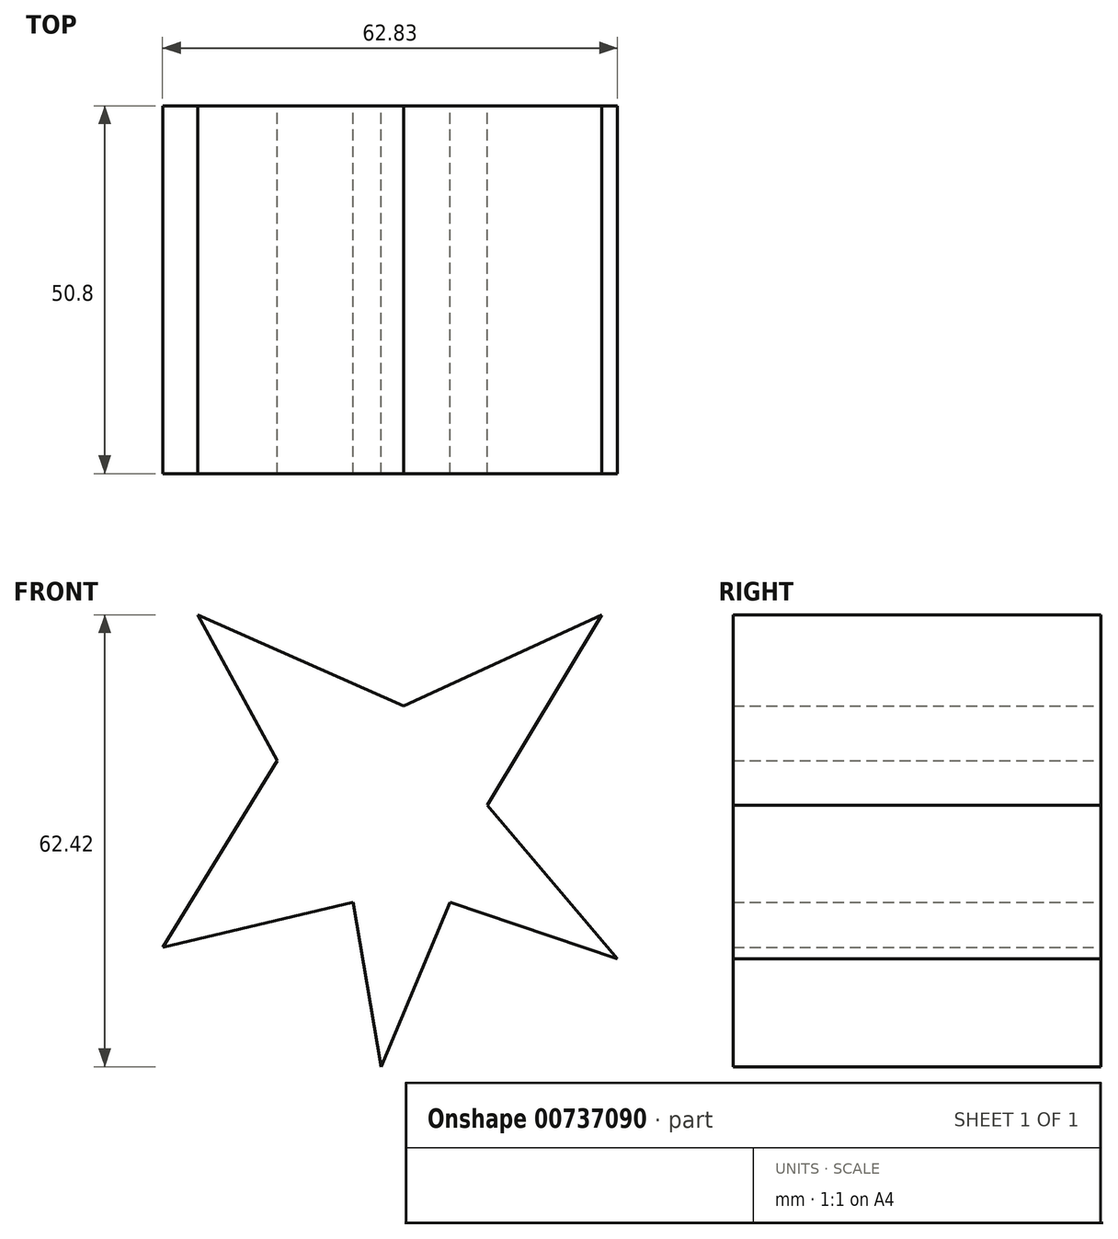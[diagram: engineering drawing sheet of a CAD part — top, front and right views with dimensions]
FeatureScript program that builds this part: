
annotation { "Feature Type Name" : "Feature", "Feature Type Description" : "" }
export const myFeature = defineFeature(function(context is Context, id is Id, definition is map)
    precondition{}
    {
        {
            var Q0;
            Q0=qCreatedBy(makeId("Front.planeOp"),FACE);
            var sketch = newSketch(context, id + "F0", { "sketchPlane" : qUnion([Q0])});
            skLineSegment(sketch, "E0", {"start": v(0, 0) * mm, "end": v(9.53, 22.69) * mm});
            skLineSegment(sketch, "E1", {"start": v(9.53, 22.69) * mm, "end": v(32.62, 14.9) * mm});
            skLineSegment(sketch, "E2", {"start": v(32.62, 14.9) * mm, "end": v(14.63, 36.11) * mm});
            skLineSegment(sketch, "E3", {"start": v(14.63, 36.11) * mm, "end": v(30.47, 62.42) * mm});
            skLineSegment(sketch, "E4", {"start": v(30.47, 62.42) * mm, "end": v(3.09, 49.8) * mm});
            skLineSegment(sketch, "E5", {"start": v(3.09, 49.8) * mm, "end": v(-25.37, 62.42) * mm});
            skLineSegment(sketch, "E6", {"start": v(-25.37, 62.42) * mm, "end": v(-14.36, 42.29) * mm});
            skLineSegment(sketch, "E7", {"start": v(-14.36, 42.29) * mm, "end": v(-30.2, 16.51) * mm});
            skLineSegment(sketch, "E8", {"start": v(-30.2, 16.51) * mm, "end": v(-3.9, 22.69) * mm});
            skLineSegment(sketch, "E9", {"start": v(-3.9, 22.69) * mm, "end": v(0, 0) * mm});
            skSolve(sketch);
        }
        {
            var Q0;
            Q0=makeQuery(id+"F0.imprint","IMPRINT",FACE,{"disambiguationData":[TD([[makeQuery(id+"F0.imprint","IMPRINT",EDGE,{"derivedFrom":sQuery(id+"F0.wireOp",EDGE,"E0")}),1.0]])]});
            extrude(context, id + "F1", {"entities" : qUnion([Q0]), "endBound" : BoundingType.SYMMETRIC, "depth" : 50.8 * mm, "offsetDistance" : 25.4 * mm});
        }
    });
